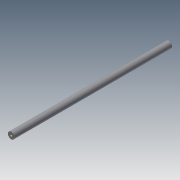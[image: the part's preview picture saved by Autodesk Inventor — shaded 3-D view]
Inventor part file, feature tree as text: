
AUTODESK INVENTOR PART (.ipt)
format: ipt  version: 2015 (Build 190159000, 159)  size: 71,680 bytes
history: native  units: mm
features: sketch x2, extrude x1
ambient origin geometry x8: Origin, YZ Plane, XZ Plane, XY Plane, X Axis, Y Axis, Z Axis, Center Point
bodies: Solid1 (feature_tree)
feature tree (3):
  extrude  "Extrusion1"  Depth=150.0mm TaperAngle=0.0deg
  sketch  "Sketch2"  dims[d3=90.0mm d4=0.0mm]
  sketch  "Sketch1"  dims[d0=10.0mm d1=150.0mm d2=0.0mm]
